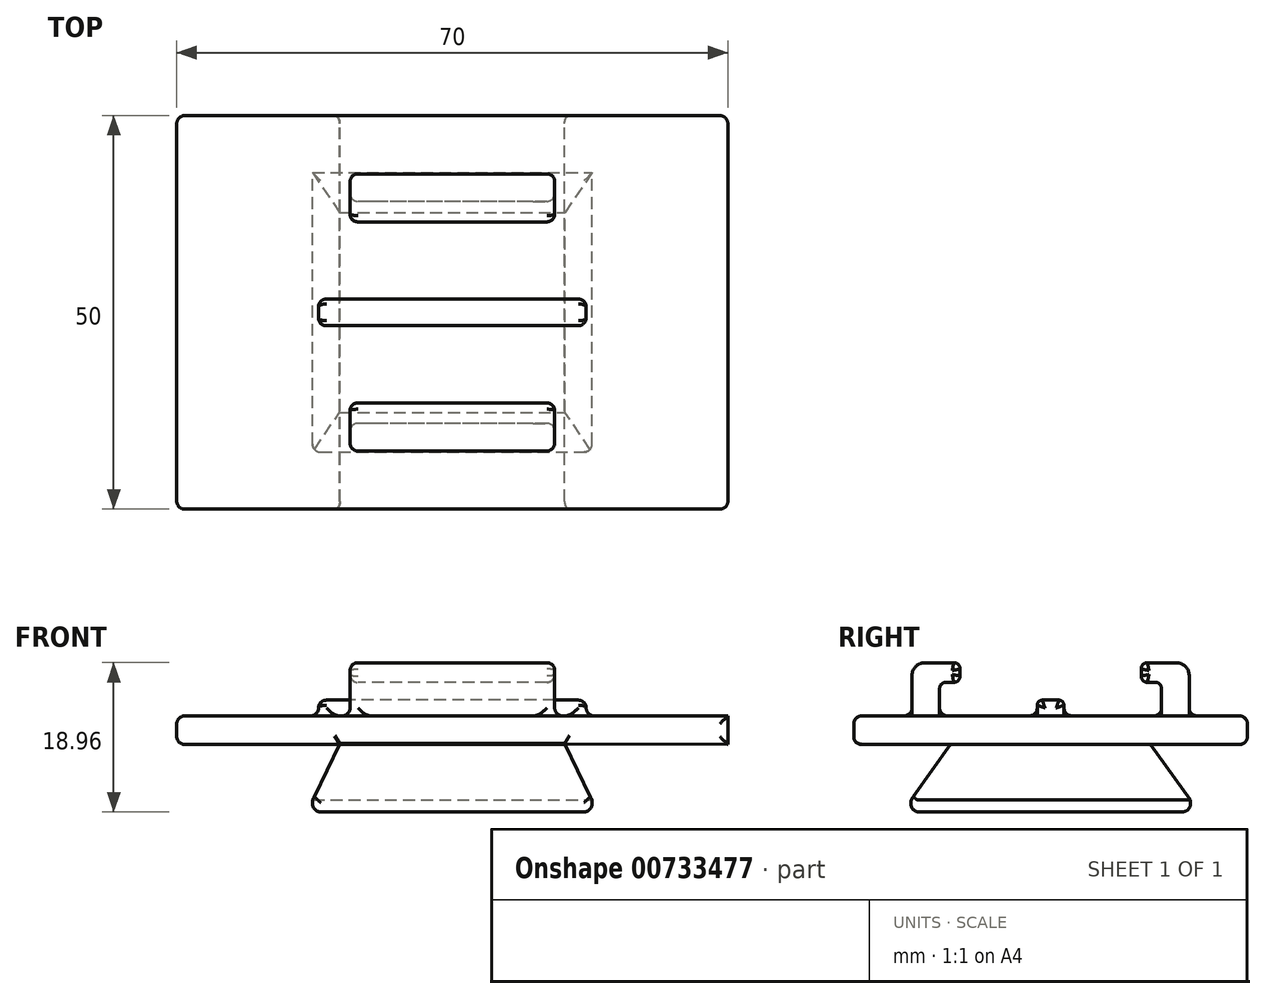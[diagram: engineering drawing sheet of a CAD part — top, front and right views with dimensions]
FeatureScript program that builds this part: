
annotation { "Feature Type Name" : "Feature", "Feature Type Description" : "" }
export const myFeature = defineFeature(function(context is Context, id is Id, definition is map)
    precondition{}
    {
        {
            var Q0;
            Q0=qCreatedBy(makeId("Front.planeOp"),FACE);
            var sketch = newSketch(context, id + "F0", { "sketchPlane" : qUnion([Q0])});
            skLineSegment(sketch, "E0.bottom", {"start": v(-14.25, 4.35) * mm, "end": v(14.25, 4.35) * mm});
            skLineSegment(sketch, "E0.top", {"start": v(-17.75, -4.35) * mm, "end": v(17.75, -4.35) * mm});
            skLineSegment(sketch, "E0.left", {"start": v(-17.75, 4.35) * mm, "end": v(-17.75, 4.31) * mm});
            skLineSegment(sketch, "E0.right", {"start": v(17.75, 4.35) * mm, "end": v(17.75, 4.31) * mm});
            skPoint(sketch, "E0.middle", {"position": v(0, 0) * mm});
            skLineSegment(sketch, "E1.bottom", {"start": v(-35, 7.85) * mm, "end": v(35, 7.85) * mm});
            skLineSegment(sketch, "E1.left", {"start": v(-35, 7.85) * mm, "end": v(-35, 4.21) * mm});
            skLineSegment(sketch, "E1.right", {"start": v(35, 7.85) * mm, "end": v(35, 4.21) * mm});
            skLineSegment(sketch, "E2.top", {"start": v(-17.75, -2.85) * mm, "end": v(17.75, -2.85) * mm});
            skLineSegment(sketch, "E2.left", {"start": v(-17.75, -4.35) * mm, "end": v(-17.75, -2.85) * mm});
            skLineSegment(sketch, "E2.right", {"start": v(17.75, -4.35) * mm, "end": v(17.75, -2.85) * mm});
            skLineSegment(sketch, "E3.top", {"start": v(-14.25, -4.35) * mm, "end": v(14.25, -4.35) * mm});
            skLineSegment(sketch, "E3.left", {"start": v(-14.25, 4.35) * mm, "end": v(-14.25, 4.31) * mm});
            skLineSegment(sketch, "E3.right", {"start": v(14.25, 4.35) * mm, "end": v(14.25, 4.31) * mm});
            skLineSegment(sketch, "E4", {"start": v(14.25, 4.35) * mm, "end": v(17.75, -2.85) * mm});
            skLineSegment(sketch, "E5", {"start": v(-14.25, 4.35) * mm, "end": v(-17.75, -2.85) * mm});
            skPoint(sketch, "E1.top.start.orphan", {"position": v(-35, -7.85) * mm});
            skPoint(sketch, "E6.orphan", {"position": v(35, -7.85) * mm});
            skLineSegment(sketch, "E7.trimOffspring", {"start": v(17.75, -2.85) * mm, "end": v(17.75, -4.35) * mm});
            skLineSegment(sketch, "E8.trimOffspring", {"start": v(-17.75, -2.85) * mm, "end": v(-17.75, -4.35) * mm});
            skLineSegment(sketch, "E9.trimOffspring", {"start": v(-14.27, 4.31) * mm, "end": v(14.27, 4.31) * mm});
            skLineSegment(sketch, "E10", {"start": v(35, 4.21) * mm, "end": v(-35, 4.21) * mm});
            skLineSegment(sketch, "E11", {"start": v(33.93, 4.21) * mm, "end": v(-14.25, 4.35) * mm});
            skLineSegment(sketch, "E12", {"start": v(14.27, 4.31) * mm, "end": v(35, 4.21) * mm});
            skLineSegment(sketch, "E13", {"start": v(35, 4.21) * mm, "end": v(35, 7.85) * mm});
            skLineSegment(sketch, "E14", {"start": v(35, 7.85) * mm, "end": v(-35, 7.85) * mm});
            skSolve(sketch);
        }
        {
            var Q0;
            {var subQ4=sQuery(id+"F0.wireOp",EDGE,"E2.top");Q0=makeQuery(id+"F0.imprint","IMPRINT",FACE,{"disambiguationData":[TD([[makeQuery(id+"F0.imprint","IMPRINT",EDGE,{"derivedFrom":subQ4}),1.0]])]});}
            var Q1;
            Q1=makeQuery(id+"F0.imprint","IMPRINT",FACE,{"disambiguationData":[TD([[makeQuery(id+"F0.imprint","IMPRINT",EDGE,{"derivedFrom":sQuery(id+"F0.wireOp",EDGE,"E2.top")}),-1.0]])]});
            extrude(context, id + "F1", {"entities" : qUnion([Q0, Q1]), "depth" : 35.5 * mm, "offsetDistance" : 25 * mm, "symmetric" : true});
        }
        {
            var Q0;
            {var subQ2=sQuery(id+"F0.wireOp",EDGE,"E0.bottom");Q0=makeQuery(id+"F0.imprint","IMPRINT",FACE,{"disambiguationData":[TD([[makeQuery(id+"F0.imprint","IMPRINT",EDGE,{"derivedFrom":subQ2}),1.0]])]});}
            extrude(context, id + "F2", {"entities" : qUnion([Q0]), "operationType" : NewBodyOperationType.ADD, "depth" : 50 * mm, "offsetDistance" : 25 * mm, "symmetric" : true});
        }
        {
            var Q0;
            Q0=qCreatedBy(makeId("Right.planeOp"),FACE);
            var sketch = newSketch(context, id + "F3", { "sketchPlane" : qUnion([Q0])});
            skLineSegment(sketch, "E15", {"start": v(17.6, 7.85) * mm, "end": v(17.6, 13) * mm});
            skLineSegment(sketch, "E16", {"start": v(16, 14.6) * mm, "end": v(12.3, 14.6) * mm});
            skLineSegment(sketch, "E17", {"start": v(11.5, 13.8) * mm, "end": v(11.5, 12.9) * mm});
            skLineSegment(sketch, "E18", {"start": v(12.3, 12.1) * mm, "end": v(13.3, 12.1) * mm});
            skLineSegment(sketch, "E19", {"start": v(14.1, 11.3) * mm, "end": v(14.1, 7.85) * mm});
            skLineSegment(sketch, "E20.MirrorCS", {"start": v(0, 7.85) * mm, "end": v(-1.7, 7.85) * mm});
            skPoint(sketch, "E21.MirrorCS.end.orphan", {"position": v(0, 9.85) * mm});
            skPoint(sketch, "E21.MirrorCS.start.orphan", {"position": v(0, 7.85) * mm});
            skLineSegment(sketch, "E22.trimOffspring", {"start": v(14.1, 7.85) * mm, "end": v(17.6, 7.85) * mm});
            skLineSegment(sketch, "E23.MirrorCS", {"start": v(0, 9.85) * mm, "end": v(1.06, 9.85) * mm});
            skLineSegment(sketch, "E24.MirrorCS", {"start": v(1.7, 9.21) * mm, "end": v(1.7, 7.85) * mm});
            skLineSegment(sketch, "E25.MirrorCS", {"start": v(0, 7.85) * mm, "end": v(1.7, 7.85) * mm});
            skPoint(sketch, "E26.visualSharp", {"position": v(14.1, 12.1) * mm});
            skArc(sketch, "E26.filletArc", {"start": v(14.1, 11.3) * mm, "mid": v(13.87, 11.87) * mm, "end": v(13.3, 12.1) * mm});
            skPoint(sketch, "E27.visualSharp", {"position": v(11.5, 12.1) * mm});
            skArc(sketch, "E27.filletArc", {"start": v(11.5, 12.9) * mm, "mid": v(11.73, 12.34) * mm, "end": v(12.3, 12.1) * mm});
            skPoint(sketch, "E28.visualSharp", {"position": v(11.5, 14.6) * mm});
            skArc(sketch, "E28.filletArc", {"start": v(12.3, 14.6) * mm, "mid": v(11.73, 14.37) * mm, "end": v(11.5, 13.8) * mm});
            skPoint(sketch, "E29.visualSharp", {"position": v(17.6, 14.6) * mm});
            skArc(sketch, "E29.filletArc", {"start": v(17.6, 13) * mm, "mid": v(17.13, 14.14) * mm, "end": v(16, 14.6) * mm});
            skPoint(sketch, "E30.visualSharp", {"position": v(1.7, 9.85) * mm});
            skArc(sketch, "E30.filletArc", {"start": v(1.7, 9.21) * mm, "mid": v(1.51, 9.66) * mm, "end": v(1.06, 9.85) * mm});
            skLineSegment(sketch, "E31.MirrorCS", {"start": v(0, 9.85) * mm, "end": v(-1.06, 9.85) * mm});
            skArc(sketch, "E32.MirrorCS", {"start": v(-1.7, 9.21) * mm, "mid": v(-1.51, 9.66) * mm, "end": v(-1.06, 9.85) * mm});
            skLineSegment(sketch, "E33.MirrorCS", {"start": v(-1.7, 9.21) * mm, "end": v(-1.7, 7.85) * mm});
            skLineSegment(sketch, "E34.MirrorCS", {"start": v(-14.1, 11.3) * mm, "end": v(-14.1, 7.85) * mm});
            skLineSegment(sketch, "E35.MirrorCS", {"start": v(-17.6, 7.85) * mm, "end": v(-17.6, 13) * mm});
            skArc(sketch, "E36.MirrorCS", {"start": v(-17.6, 13) * mm, "mid": v(-17.13, 14.14) * mm, "end": v(-16, 14.6) * mm});
            skLineSegment(sketch, "E37.MirrorCS", {"start": v(-16, 14.6) * mm, "end": v(-12.3, 14.6) * mm});
            skArc(sketch, "E38.MirrorCS", {"start": v(-12.3, 14.6) * mm, "mid": v(-11.73, 14.37) * mm, "end": v(-11.5, 13.8) * mm});
            skLineSegment(sketch, "E39.MirrorCS", {"start": v(-11.5, 13.8) * mm, "end": v(-11.5, 12.9) * mm});
            skArc(sketch, "E40.MirrorCS", {"start": v(-11.5, 12.9) * mm, "mid": v(-11.73, 12.34) * mm, "end": v(-12.3, 12.1) * mm});
            skLineSegment(sketch, "E41.MirrorCS", {"start": v(-12.3, 12.1) * mm, "end": v(-13.3, 12.1) * mm});
            skArc(sketch, "E42.MirrorCS", {"start": v(-14.1, 11.3) * mm, "mid": v(-13.87, 11.87) * mm, "end": v(-13.3, 12.1) * mm});
            skLineSegment(sketch, "E43", {"start": v(-14.1, 7.85) * mm, "end": v(-17.6, 7.85) * mm});
            skSolve(sketch);
        }
        {
            var Q0;
            Q0=makeQuery(id+"F3.imprint","IMPRINT",FACE,{"disambiguationData":[TD([[makeQuery(id+"F3.imprint","IMPRINT",EDGE,{"derivedFrom":sQuery(id+"F3.wireOp",EDGE,"E15")}),1.0]])]});
            var Q1;
            Q1=makeQuery(id+"F3.imprint","IMPRINT",FACE,{"disambiguationData":[TD([[makeQuery(id+"F3.imprint","IMPRINT",EDGE,{"derivedFrom":sQuery(id+"F3.wireOp",EDGE,"E34.MirrorCS")}),-1.0]])]});
            extrude(context, id + "F4", {"entities" : qUnion([Q0, Q1]), "operationType" : NewBodyOperationType.ADD, "depth" : 26 * mm, "offsetDistance" : 25 * mm, "symmetric" : true});
        }
        {
            var Q0;
            Q0=makeQuery(id+"F3.imprint","IMPRINT",FACE,{"disambiguationData":[TD([[makeQuery(id+"F3.imprint","IMPRINT",EDGE,{"derivedFrom":sQuery(id+"F3.wireOp",EDGE,"E20.MirrorCS")}),-1.0]])]});
            extrude(context, id + "F5", {"entities" : qUnion([Q0]), "operationType" : NewBodyOperationType.ADD, "depth" : 34 * mm, "offsetDistance" : 25 * mm, "symmetric" : true});
        }
        {
            var Q0;
            Q0=qCreatedBy(makeId("Right.planeOp"),FACE);
            var sketch = newSketch(context, id + "F6", { "sketchPlane" : qUnion([Q0])});
            skPoint(sketch, "E44", {"position": v(17.75, -2.85) * mm});
            skPoint(sketch, "E45", {"position": v(17.75, 4.21) * mm});
            skPoint(sketch, "E46", {"position": v(12.7, 4.21) * mm});
            skLineSegment(sketch, "E47", {"start": v(17.75, 4.21) * mm, "end": v(17.75, -2.85) * mm});
            skLineSegment(sketch, "E48", {"start": v(17.75, -2.85) * mm, "end": v(12.7, 4.21) * mm});
            skLineSegment(sketch, "E49", {"start": v(12.7, 4.21) * mm, "end": v(17.75, 4.21) * mm});
            skLineSegment(sketch, "E50.MirrorCS", {"start": v(-12.7, 4.21) * mm, "end": v(-17.75, 4.21) * mm});
            skLineSegment(sketch, "E51.MirrorCS", {"start": v(-17.75, 4.21) * mm, "end": v(-17.75, -2.85) * mm});
            skLineSegment(sketch, "E52.MirrorCS", {"start": v(-17.75, -2.85) * mm, "end": v(-12.7, 4.21) * mm});
            skSolve(sketch);
        }
        {
            var Q0;
            Q0 = qSketchRegion(id + "F6", true);
            extrude(context, id + "F7", {"entities" : qUnion([Q0]), "operationType" : NewBodyOperationType.REMOVE, "oppositeDirection" : true, "depth" : 40 * mm, "offsetDistance" : 25 * mm, "symmetric" : true});
        }
        {
            var Q0;
            Q0=makeQuery(id+"F2.opExtrude","CAP_FACE",FACE,{"disambiguationData":[OSD([sQuery(id+"F0.wireOp",EDGE,"E0.bottom"),sQuery(id+"F0.wireOp",EDGE,"E4"),sQuery(id+"F0.wireOp",EDGE,"E5"),sQuery(id+"F0.wireOp",EDGE,"E10"),sQuery(id+"F0.wireOp",EDGE,"E1.left"),sQuery(id+"F0.wireOp",EDGE,"E12"),sQuery(id+"F0.wireOp",EDGE,"E13"),sQuery(id+"F0.wireOp",EDGE,"E14")])],"isStart":false});
            var Q1;
            Q1=makeQuery(id+"F2.opExtrude","SWEPT_FACE",FACE,{"disambiguationData":[OSD([sQuery(id+"F0.wireOp",EDGE,"E13")])]});
            var Q2;
            Q2=makeQuery(id+"F2.opExtrude","CAP_FACE",FACE,{"disambiguationData":[OSD([sQuery(id+"F0.wireOp",EDGE,"E0.bottom"),sQuery(id+"F0.wireOp",EDGE,"E4"),sQuery(id+"F0.wireOp",EDGE,"E5"),sQuery(id+"F0.wireOp",EDGE,"E10"),sQuery(id+"F0.wireOp",EDGE,"E1.left"),sQuery(id+"F0.wireOp",EDGE,"E12"),sQuery(id+"F0.wireOp",EDGE,"E13"),sQuery(id+"F0.wireOp",EDGE,"E14")])],"isStart":true});
            var Q3;
            Q3=makeQuery(id+"F2.opExtrude","SWEPT_FACE",FACE,{"disambiguationData":[OSD([sQuery(id+"F0.wireOp",EDGE,"E1.left")])]});
            var Q4;
            Q4=makeQuery(id+"F1.opExtrude","CAP_EDGE",EDGE,{"disambiguationData":[OSD([sQuery(id+"F0.wireOp",EDGE,"E5")])],"isStart":true});
            var Q5;
            Q5=makeQuery(id+"F1.opExtrude","SWEPT_FACE",FACE,{"disambiguationData":[OSD([sQuery(id+"F0.wireOp",EDGE,"E0.top"),sQuery(id+"F0.wireOp",EDGE,"E3.top")])]});
            var Q6;
            Q6=makeQuery(id+"F1.opExtrude","CAP_EDGE",EDGE,{"disambiguationData":[OSD([sQuery(id+"F0.wireOp",EDGE,"E4")])],"isStart":true});
            var Q7;
            Q7=makeQuery(id+"F1.opExtrude","CAP_EDGE",EDGE,{"disambiguationData":[OSD([sQuery(id+"F0.wireOp",EDGE,"E8.trimOffspring")])],"isStart":false});
            var Q8;
            Q8=makeQuery(id+"F1.opExtrude","CAP_EDGE",EDGE,{"disambiguationData":[OSD([sQuery(id+"F0.wireOp",EDGE,"E5")])],"isStart":false});
            var Q9;
            Q9=makeQuery(id+"F1.opExtrude","CAP_FACE",FACE,{"disambiguationData":[OSD([sQuery(id+"F0.wireOp",EDGE,"E0.top"),sQuery(id+"F0.wireOp",EDGE,"E3.top"),sQuery(id+"F0.wireOp",EDGE,"E4"),sQuery(id+"F0.wireOp",EDGE,"E5"),sQuery(id+"F0.wireOp",EDGE,"E7.trimOffspring"),sQuery(id+"F0.wireOp",EDGE,"E8.trimOffspring"),sQuery(id+"F0.wireOp",EDGE,"E10")])],"isStart":false});
            fillet(context, id + "F8", {"entities" : qUnion([Q0, Q1, Q2, Q3, Q4, Q5, Q6, Q7, Q8, Q9]), "radius" : 1 * mm, "tangentPropagation" : true, "allowEdgeOverflow" : false});
        }
        {
            var Q0;
            Q0=makeQuery(id+"F4.opExtrude","CAP_FACE",FACE,{"disambiguationData":[OSD([sQuery(id+"F3.wireOp",EDGE,"E15"),sQuery(id+"F3.wireOp",EDGE,"E16"),sQuery(id+"F3.wireOp",EDGE,"E17"),sQuery(id+"F3.wireOp",EDGE,"E18"),sQuery(id+"F3.wireOp",EDGE,"E19"),sQuery(id+"F3.wireOp",EDGE,"E22.trimOffspring"),sQuery(id+"F3.wireOp",EDGE,"E26.filletArc"),sQuery(id+"F3.wireOp",EDGE,"E27.filletArc"),sQuery(id+"F3.wireOp",EDGE,"E28.filletArc"),sQuery(id+"F3.wireOp",EDGE,"E29.filletArc")])],"isStart":true});
            var Q1;
            Q1=makeQuery(id+"F4.opExtrude","CAP_FACE",FACE,{"disambiguationData":[OSD([sQuery(id+"F3.wireOp",EDGE,"E34.MirrorCS"),sQuery(id+"F3.wireOp",EDGE,"E35.MirrorCS"),sQuery(id+"F3.wireOp",EDGE,"E36.MirrorCS"),sQuery(id+"F3.wireOp",EDGE,"E37.MirrorCS"),sQuery(id+"F3.wireOp",EDGE,"E38.MirrorCS"),sQuery(id+"F3.wireOp",EDGE,"E39.MirrorCS"),sQuery(id+"F3.wireOp",EDGE,"E40.MirrorCS"),sQuery(id+"F3.wireOp",EDGE,"E41.MirrorCS"),sQuery(id+"F3.wireOp",EDGE,"E42.MirrorCS"),sQuery(id+"F3.wireOp",EDGE,"E43")])],"isStart":true});
            var Q2;
            Q2=makeQuery(id+"F5.opExtrude","CAP_FACE",FACE,{"disambiguationData":[OSD([sQuery(id+"F3.wireOp",EDGE,"E20.MirrorCS"),sQuery(id+"F3.wireOp",EDGE,"E23.MirrorCS"),sQuery(id+"F3.wireOp",EDGE,"E24.MirrorCS"),sQuery(id+"F3.wireOp",EDGE,"E25.MirrorCS"),sQuery(id+"F3.wireOp",EDGE,"E30.filletArc"),sQuery(id+"F3.wireOp",EDGE,"E31.MirrorCS"),sQuery(id+"F3.wireOp",EDGE,"E32.MirrorCS"),sQuery(id+"F3.wireOp",EDGE,"E33.MirrorCS")])],"isStart":true});
            var Q3;
            Q3=makeQuery(id+"F4.opExtrude","CAP_FACE",FACE,{"disambiguationData":[OSD([sQuery(id+"F3.wireOp",EDGE,"E15"),sQuery(id+"F3.wireOp",EDGE,"E16"),sQuery(id+"F3.wireOp",EDGE,"E17"),sQuery(id+"F3.wireOp",EDGE,"E18"),sQuery(id+"F3.wireOp",EDGE,"E19"),sQuery(id+"F3.wireOp",EDGE,"E22.trimOffspring"),sQuery(id+"F3.wireOp",EDGE,"E26.filletArc"),sQuery(id+"F3.wireOp",EDGE,"E27.filletArc"),sQuery(id+"F3.wireOp",EDGE,"E28.filletArc"),sQuery(id+"F3.wireOp",EDGE,"E29.filletArc")])],"isStart":false});
            var Q4;
            Q4=makeQuery(id+"F5.opExtrude","CAP_FACE",FACE,{"disambiguationData":[OSD([sQuery(id+"F3.wireOp",EDGE,"E20.MirrorCS"),sQuery(id+"F3.wireOp",EDGE,"E23.MirrorCS"),sQuery(id+"F3.wireOp",EDGE,"E24.MirrorCS"),sQuery(id+"F3.wireOp",EDGE,"E25.MirrorCS"),sQuery(id+"F3.wireOp",EDGE,"E30.filletArc"),sQuery(id+"F3.wireOp",EDGE,"E31.MirrorCS"),sQuery(id+"F3.wireOp",EDGE,"E32.MirrorCS"),sQuery(id+"F3.wireOp",EDGE,"E33.MirrorCS")])],"isStart":false});
            var Q5;
            Q5=makeQuery(id+"F4.opExtrude","CAP_FACE",FACE,{"disambiguationData":[OSD([sQuery(id+"F3.wireOp",EDGE,"E34.MirrorCS"),sQuery(id+"F3.wireOp",EDGE,"E35.MirrorCS"),sQuery(id+"F3.wireOp",EDGE,"E36.MirrorCS"),sQuery(id+"F3.wireOp",EDGE,"E37.MirrorCS"),sQuery(id+"F3.wireOp",EDGE,"E38.MirrorCS"),sQuery(id+"F3.wireOp",EDGE,"E39.MirrorCS"),sQuery(id+"F3.wireOp",EDGE,"E40.MirrorCS"),sQuery(id+"F3.wireOp",EDGE,"E41.MirrorCS"),sQuery(id+"F3.wireOp",EDGE,"E42.MirrorCS"),sQuery(id+"F3.wireOp",EDGE,"E43")])],"isStart":false});
            fillet(context, id + "F9", {"entities" : qUnion([Q0, Q1, Q2, Q3, Q4, Q5]), "radius" : 1 * mm, "tangentPropagation" : true, "allowEdgeOverflow" : false});
        }
    });
